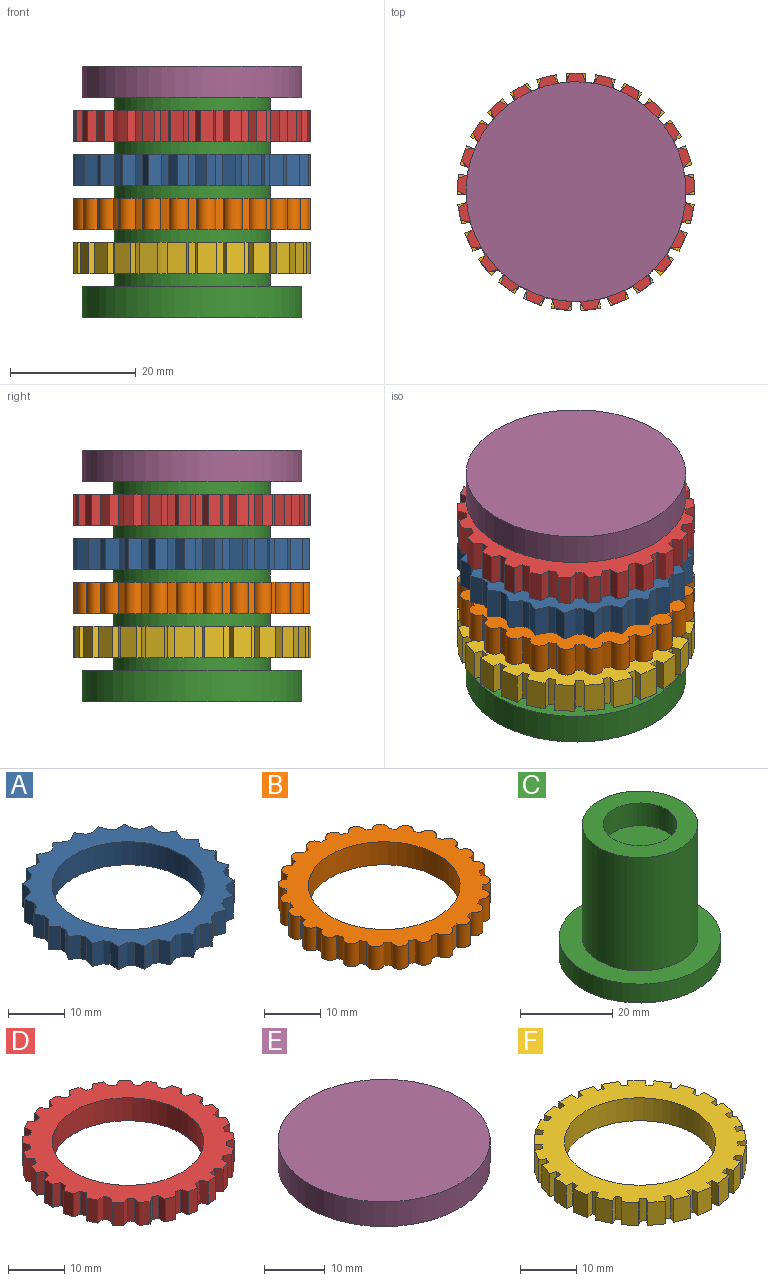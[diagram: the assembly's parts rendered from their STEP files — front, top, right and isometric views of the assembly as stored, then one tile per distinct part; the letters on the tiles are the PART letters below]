
ASSEMBLY  parts=6 mates=5
PART A: 78 faces, bbox 37.7x37.6x5 mm
  f0: plane 5x1.86mm, normal (0.5,0.87,0), area 10.8mm2, adj f1,f74,f76,f77
  f1: cylinder r=17.5mm len=5mm, axis (0,0,-1), area 6mm2, adj f0,f2,f76,f77
  f2: plane 5x2.12mm, normal (0.99,-0.17,0), area 10.8mm2, adj f1,f3,f76,f77
  f3: plane 5x2.07mm, normal (0.27,0.96,0), area 10.8mm2, adj f2,f4,f76,f77
  f4: cylinder r=17.5mm len=5mm, axis (0,0,-1), area 6mm2, adj f3,f5,f76,f77
  f5: plane 5x2.14mm, normal (1,0.08,0), area 10.8mm2, adj f4,f6,f76,f77
  f6: plane 5x2.15mm, normal (0.02,1,0), area 10.8mm2, adj f5,f7,f76,f77
  f7: cylinder r=17.5mm len=5mm, axis (0,0,-1), area 6mm2, adj f6,f8,f76,f77
  f8: plane 5x2.03mm, normal (0.94,0.33,0), area 10.8mm2, adj f7,f9,f76,f77
  f9: plane 5x2.09mm, normal (-0.23,0.97,0), area 10.8mm2, adj f8,f10,f76,f77
  f10: cylinder r=17.5mm len=5mm, axis (0,0,-1), area 6mm2, adj f9,f11,f76,f77
  f11: plane 5x1.79mm, normal (0.83,0.55,0), area 10.8mm2, adj f10,f12,f76,f77
  f12: plane 5x1.91mm, normal (-0.46,0.89,0), area 10.8mm2, adj f11,f13,f76,f77
  f13: cylinder r=17.5mm len=5mm, axis (0,0,-1), area 6mm2, adj f12,f14,f76,f77
  f14: plane 5x1.6mm, normal (0.67,0.74,0), area 10.8mm2, adj f13,f15,f76,f77
  f15: plane 5x1.6mm, normal (-0.67,0.74,0), area 10.8mm2, adj f14,f16,f76,f77
  f16: cylinder r=17.5mm len=5mm, axis (0,0,-1), area 6mm2, adj f15,f17,f76,f77
  f17: plane 5x1.91mm, normal (0.46,0.89,0), area 10.8mm2, adj f16,f18,f76,f77
  f18: plane 5x1.79mm, normal (-0.83,0.55,0), area 10.8mm2, adj f17,f19,f76,f77
  f19: cylinder r=17.5mm len=5mm, axis (0,0,-1), area 6mm2, adj f18,f20,f76,f77
  f20: plane 5x2.09mm, normal (0.23,0.97,0), area 10.8mm2, adj f19,f21,f76,f77
  f21: plane 5x2.03mm, normal (-0.94,0.33,0), area 10.8mm2, adj f20,f22,f76,f77
  f22: cylinder r=17.5mm len=5mm, axis (0,0,-1), area 6mm2, adj f21,f23,f76,f77
  f23: plane 5x2.15mm, normal (-0.02,1,0), area 10.8mm2, adj f22,f24,f76,f77
  f24: plane 5x2.14mm, normal (-1,0.08,0), area 10.8mm2, adj f23,f25,f76,f77
  f25: cylinder r=17.5mm len=5mm, axis (0,0,-1), area 6mm2, adj f24,f26,f76,f77
  f26: plane 5x2.07mm, normal (-0.27,0.96,0), area 10.8mm2, adj f25,f27,f76,f77
  f27: plane 5x2.12mm, normal (-0.99,-0.17,0), area 10.8mm2, adj f26,f28,f76,f77
  f28: cylinder r=17.5mm len=5mm, axis (0,0,-1), area 6mm2, adj f27,f29,f76,f77
  f29: plane 5x1.86mm, normal (-0.5,0.87,0), area 10.8mm2, adj f28,f30,f76,f77
  f30: plane 5x1.96mm, normal (-0.91,-0.41,0), area 10.8mm2, adj f29,f31,f76,f77
  f31: cylinder r=17.5mm len=5mm, axis (0,0,-1), area 6mm2, adj f30,f32,f76,f77
  f32: plane 5x1.54mm, normal (-0.7,0.72,0), area 10.8mm2, adj f31,f33,f76,f77
  f33: plane 5x1.68mm, normal (-0.78,-0.62,0), area 10.8mm2, adj f32,f34,f76,f77
  f34: cylinder r=17.5mm len=5mm, axis (0,0,-1), area 6mm2, adj f33,f35,f76,f77
  f35: plane 5x1.84mm, normal (-0.85,0.52,0), area 10.8mm2, adj f34,f36,f76,f77
  f36: plane 5x1.72mm, normal (-0.6,-0.8,0), area 10.8mm2, adj f35,f37,f76,f77
  f37: cylinder r=17.5mm len=5mm, axis (0,0,-1), area 6mm2, adj f36,f38,f76,f77
  f38: plane 5x2.06mm, normal (-0.96,0.29,0), area 10.8mm2, adj f37,f39,f76,f77
  f39: plane 5x1.98mm, normal (-0.39,-0.92,0), area 10.8mm2, adj f38,f40,f76,f77
  f40: cylinder r=17.5mm len=5mm, axis (0,0,-1), area 6mm2, adj f39,f41,f76,f77
  f41: plane 5x2.15mm, normal (-1,0.04,0), area 10.8mm2, adj f40,f42,f76,f77
  f42: plane 5x2.13mm, normal (-0.14,-0.99,0), area 10.8mm2, adj f41,f43,f76,f77
  f43: cylinder r=17.5mm len=5mm, axis (0,0,-1), area 6mm2, adj f42,f44,f76,f77
  f44: plane 5x2.1mm, normal (-0.98,-0.21,0), area 10.8mm2, adj f43,f45,f76,f77
  f45: plane 5x2.14mm, normal (0.11,-0.99,0), area 10.8mm2, adj f44,f46,f76,f77
  f46: cylinder r=17.5mm len=5mm, axis (0,0,-1), area 6mm2, adj f45,f47,f76,f77
  f47: plane 5x1.93mm, normal (-0.9,-0.44,0), area 10.8mm2, adj f46,f48,f76,f77
  f48: plane 5x2.02mm, normal (0.35,-0.94,0), area 10.8mm2, adj f47,f49,f76,f77
  f49: cylinder r=17.5mm len=5mm, axis (0,0,-1), area 6mm2, adj f48,f50,f76,f77
  f50: plane 5x1.63mm, normal (-0.76,-0.65,0), area 10.8mm2, adj f49,f51,f76,f77
  f51: plane 5x1.76mm, normal (0.57,-0.82,0), area 10.8mm2, adj f50,f52,f76,f77
  f52: cylinder r=17.5mm len=5mm, axis (0,0,-1), area 6mm2, adj f51,f53,f76,f77
  f53: plane 5x1.76mm, normal (-0.57,-0.82,0), area 10.8mm2, adj f52,f54,f76,f77
  f54: plane 5x1.63mm, normal (0.76,-0.65,0), area 10.8mm2, adj f53,f55,f76,f77
  f55: cylinder r=17.5mm len=5mm, axis (0,0,-1), area 6mm2, adj f54,f56,f76,f77
  f56: plane 5x2.02mm, normal (-0.35,-0.94,0), area 10.8mm2, adj f55,f57,f76,f77
  f57: plane 5x1.93mm, normal (0.9,-0.44,0), area 10.8mm2, adj f56,f58,f76,f77
  f58: cylinder r=17.5mm len=5mm, axis (0,0,-1), area 6mm2, adj f57,f59,f76,f77
  f59: plane 5x2.14mm, normal (-0.11,-0.99,0), area 10.8mm2, adj f58,f60,f76,f77
  f60: plane 5x2.1mm, normal (0.98,-0.21,0), area 10.8mm2, adj f59,f61,f76,f77
  f61: cylinder r=17.5mm len=5mm, axis (0,0,-1), area 6mm2, adj f60,f62,f76,f77
  f62: plane 5x2.13mm, normal (0.14,-0.99,0), area 10.8mm2, adj f61,f63,f76,f77
  f63: plane 5x2.15mm, normal (1,0.04,0), area 10.8mm2, adj f62,f64,f76,f77
  f64: cylinder r=17.5mm len=5mm, axis (0,0,-1), area 6mm2, adj f63,f65,f76,f77
  f65: plane 5x1.98mm, normal (0.39,-0.92,0), area 10.8mm2, adj f64,f66,f76,f77
  f66: plane 5x2.06mm, normal (0.96,0.29,0), area 10.8mm2, adj f65,f67,f76,f77
  f67: cylinder r=17.5mm len=5mm, axis (0,0,-1), area 6mm2, adj f66,f68,f76,f77
  f68: plane 5x1.72mm, normal (0.6,-0.8,0), area 10.8mm2, adj f67,f69,f76,f77
  f69: plane 5x1.84mm, normal (0.85,0.52,0), area 10.8mm2, adj f68,f70,f76,f77
  f70: cylinder r=17.5mm len=5mm, axis (0,0,-1), area 6mm2, adj f69,f71,f76,f77
  f71: plane 5x1.68mm, normal (0.78,-0.62,0), area 10.8mm2, adj f70,f72,f76,f77
  f72: plane 5x1.54mm, normal (0.7,0.72,0), area 10.8mm2, adj f71,f73,f76,f77
  f73: cylinder r=17.5mm len=5mm, axis (0,0,-1), area 6mm2, adj f72,f74,f76,f77
  f74: plane 5x1.96mm, normal (0.91,-0.41,0), area 10.8mm2, adj f0,f73,f76,f77
  f75: cylinder r=13.5mm len=27mm, axis (0,0,-1), area 424.1mm2, adj f76,f77
  f76: plane 37.66x37.59mm, normal (0,0,1), area 443.2mm2, adj f0,f1,f2,f3,f4,f5,f6,f7
  f77: plane 37.66x37.59mm, normal (0,0,-1), area 443.2mm2, adj f0,f1,f2,f3,f4,f5,f6,f7
PART B: 53 faces, bbox 37.7x37.7x5 mm
  f0: cylinder r=17.5mm len=5mm, axis (0,0,-1), area 6.9mm2, adj f1,f50,f51,f52
  f1: cylinder r=1.51mm len=5mm, axis (0,0,-1), area 23.3mm2, adj f0,f2,f51,f52
  f2: cylinder r=17.5mm len=5mm, axis (0,0,-1), area 6.9mm2, adj f1,f3,f51,f52
  f3: cylinder r=1.51mm len=5mm, axis (0,0,-1), area 23.3mm2, adj f2,f4,f51,f52
  f4: cylinder r=17.5mm len=5mm, axis (0,0,-1), area 6.9mm2, adj f3,f5,f51,f52
  f5: cylinder r=1.51mm len=5mm, axis (0,0,-1), area 23.3mm2, adj f4,f6,f51,f52
  f6: cylinder r=17.5mm len=5mm, axis (0,0,-1), area 6.9mm2, adj f5,f7,f51,f52
  f7: cylinder r=1.51mm len=5mm, axis (0,0,-1), area 23.3mm2, adj f6,f8,f51,f52
  f8: cylinder r=17.5mm len=5mm, axis (0,0,-1), area 6.9mm2, adj f7,f9,f51,f52
  f9: cylinder r=1.51mm len=5mm, axis (0,0,-1), area 23.3mm2, adj f8,f10,f51,f52
  f10: cylinder r=17.5mm len=5mm, axis (0,0,-1), area 6.9mm2, adj f9,f11,f51,f52
  f11: cylinder r=1.51mm len=5mm, axis (0,0,-1), area 23.3mm2, adj f10,f12,f51,f52
  f12: cylinder r=17.5mm len=5mm, axis (0,0,-1), area 6.9mm2, adj f11,f13,f51,f52
  f13: cylinder r=1.51mm len=5mm, axis (0,0,-1), area 23.3mm2, adj f12,f14,f51,f52
  f14: cylinder r=17.5mm len=5mm, axis (0,0,-1), area 6.9mm2, adj f13,f15,f51,f52
  f15: cylinder r=1.51mm len=5mm, axis (0,0,-1), area 23.3mm2, adj f14,f16,f51,f52
  f16: cylinder r=17.5mm len=5mm, axis (0,0,-1), area 6.9mm2, adj f15,f17,f51,f52
  f17: cylinder r=1.51mm len=5mm, axis (0,0,-1), area 23.3mm2, adj f16,f18,f51,f52
  f18: cylinder r=17.5mm len=5mm, axis (0,0,-1), area 6.9mm2, adj f17,f19,f51,f52
  f19: cylinder r=1.51mm len=5mm, axis (0,0,-1), area 23.3mm2, adj f18,f20,f51,f52
  f20: cylinder r=17.5mm len=5mm, axis (0,0,-1), area 6.9mm2, adj f19,f21,f51,f52
  f21: cylinder r=1.51mm len=5mm, axis (0,0,-1), area 23.3mm2, adj f20,f22,f51,f52
  f22: cylinder r=17.5mm len=5mm, axis (0,0,-1), area 6.9mm2, adj f21,f23,f51,f52
  f23: cylinder r=1.51mm len=5mm, axis (0,0,-1), area 23.3mm2, adj f22,f24,f51,f52
  f24: cylinder r=17.5mm len=5mm, axis (0,0,-1), area 6.9mm2, adj f23,f25,f51,f52
  f25: cylinder r=1.51mm len=5mm, axis (0,0,-1), area 23.3mm2, adj f24,f26,f51,f52
  f26: cylinder r=17.5mm len=5mm, axis (0,0,-1), area 6.9mm2, adj f25,f27,f51,f52
  f27: cylinder r=1.51mm len=5mm, axis (0,0,-1), area 23.3mm2, adj f26,f28,f51,f52
  f28: cylinder r=17.5mm len=5mm, axis (0,0,-1), area 6.9mm2, adj f27,f29,f51,f52
  f29: cylinder r=1.51mm len=5mm, axis (0,0,-1), area 23.3mm2, adj f28,f30,f51,f52
  f30: cylinder r=17.5mm len=5mm, axis (0,0,-1), area 6.9mm2, adj f29,f31,f51,f52
  f31: cylinder r=1.51mm len=5mm, axis (0,0,-1), area 23.3mm2, adj f30,f32,f51,f52
  f32: cylinder r=17.5mm len=5mm, axis (0,0,-1), area 6.9mm2, adj f31,f33,f51,f52
  f33: cylinder r=1.51mm len=5mm, axis (0,0,-1), area 23.3mm2, adj f32,f34,f51,f52
  f34: cylinder r=17.5mm len=5mm, axis (0,0,-1), area 6.9mm2, adj f33,f35,f51,f52
  f35: cylinder r=1.51mm len=5mm, axis (0,0,-1), area 23.3mm2, adj f34,f36,f51,f52
  f36: cylinder r=17.5mm len=5mm, axis (0,0,-1), area 6.9mm2, adj f35,f37,f51,f52
  f37: cylinder r=1.51mm len=5mm, axis (0,0,-1), area 23.3mm2, adj f36,f38,f51,f52
  f38: cylinder r=17.5mm len=5mm, axis (0,0,-1), area 6.9mm2, adj f37,f39,f51,f52
  f39: cylinder r=1.51mm len=5mm, axis (0,0,-1), area 23.3mm2, adj f38,f40,f51,f52
  f40: cylinder r=17.5mm len=5mm, axis (0,0,-1), area 6.9mm2, adj f39,f41,f51,f52
  f41: cylinder r=1.51mm len=5mm, axis (0,0,-1), area 23.3mm2, adj f40,f42,f51,f52
  f42: cylinder r=17.5mm len=5mm, axis (0,0,-1), area 6.9mm2, adj f41,f43,f51,f52
  f43: cylinder r=1.51mm len=5mm, axis (0,0,-1), area 23.3mm2, adj f42,f44,f51,f52
  f44: cylinder r=17.5mm len=5mm, axis (0,0,-1), area 6.9mm2, adj f43,f45,f51,f52
  f45: cylinder r=1.51mm len=5mm, axis (0,0,-1), area 23.3mm2, adj f44,f46,f51,f52
  f46: cylinder r=17.5mm len=5mm, axis (0,0,-1), area 6.9mm2, adj f45,f47,f51,f52
  f47: cylinder r=1.51mm len=5mm, axis (0,0,-1), area 23.3mm2, adj f46,f48,f51,f52
  f48: cylinder r=17.5mm len=5mm, axis (0,0,-1), area 6.9mm2, adj f47,f50,f51,f52
  f49: cylinder r=13.5mm len=27mm, axis (0,0,-1), area 424.1mm2, adj f51,f52
  f50: cylinder r=1.51mm len=5mm, axis (0,0,-1), area 23.3mm2, adj f0,f48,f51,f52
  f51: plane 37.74x37.68mm, normal (0,0,1), area 472.5mm2, adj f0,f1,f2,f3,f4,f5,f6,f7
  f52: plane 37.74x37.68mm, normal (0,0,-1), area 472.5mm2, adj f0,f1,f2,f3,f4,f5,f6,f7
PART C: 7 faces, bbox 35x35x35 mm
  f0: cylinder r=17.5mm len=35mm, axis (0,0,-1), area 549.8mm2, adj f1,f2
  f1: plane 35x35mm, normal (0,0,1), area 471.2mm2, adj f0,f3
  f2: plane 35x35mm, normal (0,0,-1), area 962.1mm2, adj f0
  f3: cylinder r=12.5mm len=30mm, axis (0,0,-1), area 2356.2mm2, adj f1,f4
  f4: plane 25x25mm, normal (0,0,1), area 289.8mm2, adj f3,f5
  f5: cylinder r=8mm len=16mm, axis (0,0,1), area 301.6mm2, adj f4,f6
  f6: plane 16x16mm, normal (0,0,1), area 201.1mm2, adj f5
PART D: 103 faces, bbox 37.8x37.7x5 mm
  f0: plane 5x1.55mm, normal (0.08,1,0), area 7.8mm2, adj f1,f99,f101,f102
  f1: cylinder r=17.5mm len=5mm, axis (0,0,-1), area 6.1mm2, adj f0,f2,f101,f102
  f2: plane 5x1.27mm, normal (0.82,-0.58,0), area 7.8mm2, adj f1,f3,f101,f102
  f3: plane 5x1.67mm, normal (0.84,0.54,0), area 9.9mm2, adj f2,f4,f101,f102
  f4: plane 5x1.53mm, normal (-0.17,0.99,0), area 7.8mm2, adj f3,f5,f101,f102
  f5: cylinder r=17.5mm len=5mm, axis (0,0,-1), area 6.1mm2, adj f4,f6,f101,f102
  f6: plane 5x1.46mm, normal (0.94,-0.35,0), area 7.8mm2, adj f5,f7,f101,f102
  f7: plane 5x1.44mm, normal (0.68,0.73,0), area 9.9mm2, adj f6,f8,f101,f102
  f8: plane 5x1.42mm, normal (-0.41,0.91,0), area 7.8mm2, adj f7,f9,f101,f102
  f9: cylinder r=17.5mm len=5mm, axis (0,0,-1), area 6.1mm2, adj f8,f10,f101,f102
  f10: plane 5x1.55mm, normal (0.99,-0.11,0), area 7.8mm2, adj f9,f11,f101,f102
  f11: plane 5x1.73mm, normal (0.48,0.88,0), area 9.9mm2, adj f10,f12,f101,f102
  f12: plane 5x1.21mm, normal (-0.63,0.78,0), area 7.8mm2, adj f11,f13,f101,f102
  f13: cylinder r=17.5mm len=5mm, axis (0,0,-1), area 6.1mm2, adj f12,f14,f101,f102
  f14: plane 5x1.54mm, normal (0.99,0.14,0), area 7.8mm2, adj f13,f15,f101,f102
  f15: plane 5x1.91mm, normal (0.25,0.97,0), area 9.9mm2, adj f14,f16,f101,f102
  f16: plane 5x1.24mm, normal (-0.8,0.6,0), area 7.8mm2, adj f15,f17,f101,f102
  f17: cylinder r=17.5mm len=5mm, axis (0,0,-1), area 6.1mm2, adj f16,f18,f101,f102
  f18: plane 5x1.44mm, normal (0.92,0.38,0), area 7.8mm2, adj f17,f19,f101,f102
  f19: plane 5x1.98mm, normal (0,1,0), area 9.9mm2, adj f18,f20,f101,f102
  f20: plane 5x1.44mm, normal (-0.92,0.38,0), area 7.8mm2, adj f19,f21,f101,f102
  f21: cylinder r=17.5mm len=5mm, axis (0,0,-1), area 6.1mm2, adj f20,f22,f101,f102
  f22: plane 5x1.24mm, normal (0.8,0.6,0), area 7.8mm2, adj f21,f23,f101,f102
  f23: plane 5x1.91mm, normal (-0.25,0.97,0), area 9.9mm2, adj f22,f24,f101,f102
  f24: plane 5x1.54mm, normal (-0.99,0.14,0), area 7.8mm2, adj f23,f25,f101,f102
  f25: cylinder r=17.5mm len=5mm, axis (0,0,-1), area 6.1mm2, adj f24,f26,f101,f102
  f26: plane 5x1.21mm, normal (0.63,0.78,0), area 7.8mm2, adj f25,f27,f101,f102
  f27: plane 5x1.73mm, normal (-0.48,0.88,0), area 9.9mm2, adj f26,f28,f101,f102
  f28: plane 5x1.55mm, normal (-0.99,-0.11,0), area 7.8mm2, adj f27,f29,f101,f102
  f29: cylinder r=17.5mm len=5mm, axis (0,0,-1), area 6.1mm2, adj f28,f30,f101,f102
  f30: plane 5x1.42mm, normal (0.41,0.91,0), area 7.8mm2, adj f29,f31,f101,f102
  f31: plane 5x1.44mm, normal (-0.68,0.73,0), area 9.9mm2, adj f30,f32,f101,f102
  f32: plane 5x1.46mm, normal (-0.94,-0.35,0), area 7.8mm2, adj f31,f33,f101,f102
  f33: cylinder r=17.5mm len=5mm, axis (0,0,-1), area 6.1mm2, adj f32,f34,f101,f102
  f34: plane 5x1.53mm, normal (0.17,0.99,0), area 7.8mm2, adj f33,f35,f101,f102
  f35: plane 5x1.67mm, normal (-0.84,0.54,0), area 9.9mm2, adj f34,f36,f101,f102
  f36: plane 5x1.27mm, normal (-0.82,-0.58,0), area 7.8mm2, adj f35,f37,f101,f102
  f37: cylinder r=17.5mm len=5mm, axis (0,0,-1), area 6.1mm2, adj f36,f38,f101,f102
  f38: plane 5x1.55mm, normal (-0.08,1,0), area 7.8mm2, adj f37,f39,f101,f102
  f39: plane 5x1.88mm, normal (-0.95,0.31,0), area 9.9mm2, adj f38,f40,f101,f102
  f40: plane 5x1.18mm, normal (-0.65,-0.76,0), area 7.8mm2, adj f39,f41,f101,f102
  f41: cylinder r=17.5mm len=5mm, axis (0,0,-1), area 6.1mm2, adj f40,f42,f101,f102
  f42: plane 5x1.47mm, normal (-0.32,0.95,0), area 7.8mm2, adj f41,f43,f101,f102
  f43: plane 5x1.97mm, normal (-1,0.06,0), area 9.9mm2, adj f42,f44,f101,f102
  f44: plane 5x1.4mm, normal (-0.44,-0.9,0), area 7.8mm2, adj f43,f45,f101,f102
  f45: cylinder r=17.5mm len=5mm, axis (0,0,-1), area 6.1mm2, adj f44,f46,f101,f102
  f46: plane 5x1.3mm, normal (-0.55,0.84,0), area 7.8mm2, adj f45,f47,f101,f102
  f47: plane 5x1.94mm, normal (-0.98,-0.19,0), area 9.9mm2, adj f46,f48,f101,f102
  f48: plane 5x1.52mm, normal (-0.2,-0.98,0), area 7.8mm2, adj f47,f49,f101,f102
  f49: cylinder r=17.5mm len=5mm, axis (0,0,-1), area 6.1mm2, adj f48,f50,f101,f102
  f50: plane 5x1.15mm, normal (-0.74,0.67,0), area 7.8mm2, adj f49,f51,f101,f102
  f51: plane 5x1.79mm, normal (-0.9,-0.43,0), area 9.9mm2, adj f50,f52,f101,f102
  f52: plane 5x1.55mm, normal (0.05,-1,0), area 7.8mm2, adj f51,f53,f101,f102
  f53: cylinder r=17.5mm len=5mm, axis (0,0,-1), area 6.1mm2, adj f52,f54,f101,f102
  f54: plane 5x1.37mm, normal (-0.88,0.47,0), area 7.8mm2, adj f53,f55,f101,f102
  f55: plane 5x1.52mm, normal (-0.77,-0.64,0), area 9.9mm2, adj f54,f56,f101,f102
  f56: plane 5x1.49mm, normal (0.29,-0.96,0), area 7.8mm2, adj f55,f57,f101,f102
  f57: cylinder r=17.5mm len=5mm, axis (0,0,-1), area 6.1mm2, adj f56,f58,f101,f102
  f58: plane 5x1.51mm, normal (-0.97,0.23,0), area 7.8mm2, adj f57,f59,f101,f102
  f59: plane 5x1.6mm, normal (-0.59,-0.81,0), area 9.9mm2, adj f58,f60,f101,f102
  f60: plane 5x1.33mm, normal (0.52,-0.85,0), area 7.8mm2, adj f59,f61,f101,f102
  f61: cylinder r=17.5mm len=5mm, axis (0,0,-1), area 6.1mm2, adj f60,f62,f101,f102
  f62: plane 5x1.56mm, normal (-1,-0.02,0), area 7.8mm2, adj f61,f63,f101,f102
  f63: plane 5x1.84mm, normal (-0.37,-0.93,0), area 9.9mm2, adj f62,f64,f101,f102
  f64: plane 5x1.12mm, normal (0.72,-0.7,0), area 7.8mm2, adj f63,f65,f101,f102
  f65: cylinder r=17.5mm len=5mm, axis (0,0,-1), area 6.1mm2, adj f64,f66,f101,f102
  f66: plane 5x1.5mm, normal (-0.96,-0.26,0), area 7.8mm2, adj f65,f67,f101,f102
  f67: plane 5x1.96mm, normal (-0.13,-0.99,0), area 9.9mm2, adj f66,f68,f101,f102
  f68: plane 5x1.35mm, normal (0.87,-0.5,0), area 7.8mm2, adj f67,f69,f101,f102
  f69: cylinder r=17.5mm len=5mm, axis (0,0,-1), area 6.1mm2, adj f68,f70,f101,f102
  f70: plane 5x1.35mm, normal (-0.87,-0.5,0), area 7.8mm2, adj f69,f71,f101,f102
  f71: plane 5x1.96mm, normal (0.13,-0.99,0), area 9.9mm2, adj f70,f72,f101,f102
  f72: plane 5x1.5mm, normal (0.96,-0.26,0), area 7.8mm2, adj f71,f73,f101,f102
  f73: cylinder r=17.5mm len=5mm, axis (0,0,-1), area 6.1mm2, adj f72,f74,f101,f102
  f74: plane 5x1.12mm, normal (-0.72,-0.7,0), area 7.8mm2, adj f73,f75,f101,f102
  f75: plane 5x1.84mm, normal (0.37,-0.93,0), area 9.9mm2, adj f74,f76,f101,f102
  f76: plane 5x1.56mm, normal (1,-0.02,0), area 7.8mm2, adj f75,f77,f101,f102
  f77: cylinder r=17.5mm len=5mm, axis (0,0,-1), area 6.1mm2, adj f76,f78,f101,f102
  f78: plane 5x1.33mm, normal (-0.52,-0.85,0), area 7.8mm2, adj f77,f79,f101,f102
  f79: plane 5x1.6mm, normal (0.59,-0.81,0), area 9.9mm2, adj f78,f80,f101,f102
  f80: plane 5x1.51mm, normal (0.97,0.23,0), area 7.8mm2, adj f79,f81,f101,f102
  f81: cylinder r=17.5mm len=5mm, axis (0,0,-1), area 6.1mm2, adj f80,f82,f101,f102
  f82: plane 5x1.49mm, normal (-0.29,-0.96,0), area 7.8mm2, adj f81,f83,f101,f102
  f83: plane 5x1.52mm, normal (0.77,-0.64,0), area 9.9mm2, adj f82,f84,f101,f102
  f84: plane 5x1.37mm, normal (0.88,0.47,0), area 7.8mm2, adj f83,f85,f101,f102
  f85: cylinder r=17.5mm len=5mm, axis (0,0,-1), area 6.1mm2, adj f84,f86,f101,f102
  f86: plane 5x1.55mm, normal (-0.05,-1,0), area 7.8mm2, adj f85,f87,f101,f102
  f87: plane 5x1.79mm, normal (0.9,-0.43,0), area 9.9mm2, adj f86,f88,f101,f102
  f88: plane 5x1.15mm, normal (0.74,0.67,0), area 7.8mm2, adj f87,f89,f101,f102
  f89: cylinder r=17.5mm len=5mm, axis (0,0,-1), area 6.1mm2, adj f88,f90,f101,f102
  f90: plane 5x1.52mm, normal (0.2,-0.98,0), area 7.8mm2, adj f89,f91,f101,f102
  f91: plane 5x1.94mm, normal (0.98,-0.19,0), area 9.9mm2, adj f90,f92,f101,f102
  f92: plane 5x1.3mm, normal (0.55,0.84,0), area 7.8mm2, adj f91,f93,f101,f102
  f93: cylinder r=17.5mm len=5mm, axis (0,0,-1), area 6.1mm2, adj f92,f94,f101,f102
  f94: plane 5x1.4mm, normal (0.44,-0.9,0), area 7.8mm2, adj f93,f95,f101,f102
  f95: plane 5x1.97mm, normal (1,0.06,0), area 9.9mm2, adj f94,f96,f101,f102
  f96: plane 5x1.47mm, normal (0.32,0.95,0), area 7.8mm2, adj f95,f97,f101,f102
  f97: cylinder r=17.5mm len=5mm, axis (0,0,-1), area 6.1mm2, adj f96,f98,f101,f102
  f98: plane 5x1.18mm, normal (0.65,-0.76,0), area 7.8mm2, adj f97,f99,f101,f102
  f99: plane 5x1.88mm, normal (0.95,0.31,0), area 9.9mm2, adj f0,f98,f101,f102
  f100: cylinder r=13.5mm len=27mm, axis (0,0,-1), area 424.1mm2, adj f101,f102
  f101: plane 37.78x37.71mm, normal (0,0,1), area 478.2mm2, adj f0,f1,f2,f3,f4,f5,f6,f7
  f102: plane 37.78x37.71mm, normal (0,0,-1), area 478.2mm2, adj f0,f1,f2,f3,f4,f5,f6,f7
PART E: 5 faces, bbox 35x35x10 mm
  f0: cylinder r=7.85mm len=15.7mm, axis (0,0,1), area 246.6mm2, adj f1,f4
  f1: plane 15.7x15.7mm, normal (0,0,-1), area 193.6mm2, adj f0
  f2: cylinder r=17.5mm len=35mm, axis (0,0,-1), area 549.8mm2, adj f3,f4
  f3: plane 35x35mm, normal (0,0,1), area 962.1mm2, adj f2
  f4: plane 35x35mm, normal (0,0,-1), area 768.5mm2, adj f0,f2
PART F: 103 faces, bbox 37.9x37.8x5 mm
  f0: plane 5x1.37mm, normal (-0.31,0.95,0), area 7.2mm2, adj f1,f99,f101,f102
  f1: cylinder r=17.5mm len=5mm, axis (0,0,-1), area 6.2mm2, adj f0,f2,f101,f102
  f2: plane 5x1.21mm, normal (0.54,-0.84,0), area 7.2mm2, adj f1,f3,f101,f102
  f3: plane 5x2.66mm, normal (0.84,0.54,0), area 15.7mm2, adj f2,f4,f101,f102
  f4: plane 5x1.21mm, normal (-0.54,0.84,0), area 7.2mm2, adj f3,f5,f101,f102
  f5: cylinder r=17.5mm len=5mm, axis (0,0,-1), area 6.2mm2, adj f4,f6,f101,f102
  f6: plane 5x1.05mm, normal (0.73,-0.68,0), area 7.2mm2, adj f5,f7,f101,f102
  f7: plane 5x2.3mm, normal (0.68,0.73,0), area 15.7mm2, adj f6,f8,f101,f102
  f8: plane 5x1.05mm, normal (-0.73,0.68,0), area 7.2mm2, adj f7,f9,f101,f102
  f9: cylinder r=17.5mm len=5mm, axis (0,0,-1), area 6.2mm2, adj f8,f10,f101,f102
  f10: plane 5x1.26mm, normal (0.88,-0.48,0), area 7.2mm2, adj f9,f11,f101,f102
  f11: plane 5x2.76mm, normal (0.48,0.88,0), area 15.7mm2, adj f10,f12,f101,f102
  f12: plane 5x1.26mm, normal (-0.88,0.48,0), area 7.2mm2, adj f11,f13,f101,f102
  f13: cylinder r=17.5mm len=5mm, axis (0,0,-1), area 6.2mm2, adj f12,f14,f101,f102
  f14: plane 5x1.39mm, normal (0.97,-0.25,0), area 7.2mm2, adj f13,f15,f101,f102
  f15: plane 5x3.05mm, normal (0.25,0.97,0), area 15.7mm2, adj f14,f16,f101,f102
  f16: plane 5x1.39mm, normal (-0.97,0.25,0), area 7.2mm2, adj f15,f17,f101,f102
  f17: cylinder r=17.5mm len=5mm, axis (0,0,-1), area 6.2mm2, adj f16,f18,f101,f102
  f18: plane 5x1.44mm, normal (1,0,0), area 7.2mm2, adj f17,f19,f101,f102
  f19: plane 5x3.15mm, normal (0,1,0), area 15.7mm2, adj f18,f20,f101,f102
  f20: plane 5x1.44mm, normal (-1,0,0), area 7.2mm2, adj f19,f21,f101,f102
  f21: cylinder r=17.5mm len=5mm, axis (0,0,-1), area 6.2mm2, adj f20,f22,f101,f102
  f22: plane 5x1.39mm, normal (0.97,0.25,0), area 7.2mm2, adj f21,f23,f101,f102
  f23: plane 5x3.05mm, normal (-0.25,0.97,0), area 15.7mm2, adj f22,f24,f101,f102
  f24: plane 5x1.39mm, normal (-0.97,-0.25,0), area 7.2mm2, adj f23,f25,f101,f102
  f25: cylinder r=17.5mm len=5mm, axis (0,0,-1), area 6.2mm2, adj f24,f26,f101,f102
  f26: plane 5x1.26mm, normal (0.88,0.48,0), area 7.2mm2, adj f25,f27,f101,f102
  f27: plane 5x2.76mm, normal (-0.48,0.88,0), area 15.7mm2, adj f26,f28,f101,f102
  f28: plane 5x1.26mm, normal (-0.88,-0.48,0), area 7.2mm2, adj f27,f29,f101,f102
  f29: cylinder r=17.5mm len=5mm, axis (0,0,-1), area 6.2mm2, adj f28,f30,f101,f102
  f30: plane 5x1.05mm, normal (0.73,0.68,0), area 7.2mm2, adj f29,f31,f101,f102
  f31: plane 5x2.3mm, normal (-0.68,0.73,0), area 15.7mm2, adj f30,f32,f101,f102
  f32: plane 5x1.05mm, normal (-0.73,-0.68,0), area 7.2mm2, adj f31,f33,f101,f102
  f33: cylinder r=17.5mm len=5mm, axis (0,0,-1), area 6.2mm2, adj f32,f34,f101,f102
  f34: plane 5x1.21mm, normal (0.54,0.84,0), area 7.2mm2, adj f33,f35,f101,f102
  f35: plane 5x2.66mm, normal (-0.84,0.54,0), area 15.7mm2, adj f34,f36,f101,f102
  f36: plane 5x1.21mm, normal (-0.54,-0.84,0), area 7.2mm2, adj f35,f37,f101,f102
  f37: cylinder r=17.5mm len=5mm, axis (0,0,-1), area 6.2mm2, adj f36,f38,f101,f102
  f38: plane 5x1.37mm, normal (0.31,0.95,0), area 7.2mm2, adj f37,f39,f101,f102
  f39: plane 5x2.99mm, normal (-0.95,0.31,0), area 15.7mm2, adj f38,f40,f101,f102
  f40: plane 5x1.37mm, normal (-0.31,-0.95,0), area 7.2mm2, adj f39,f41,f101,f102
  f41: cylinder r=17.5mm len=5mm, axis (0,0,-1), area 6.2mm2, adj f40,f42,f101,f102
  f42: plane 5x1.43mm, normal (0.06,1,0), area 7.2mm2, adj f41,f43,f101,f102
  f43: plane 5x3.14mm, normal (-1,0.06,0), area 15.7mm2, adj f42,f44,f101,f102
  f44: plane 5x1.43mm, normal (-0.06,-1,0), area 7.2mm2, adj f43,f45,f101,f102
  f45: cylinder r=17.5mm len=5mm, axis (0,0,-1), area 6.2mm2, adj f44,f46,f101,f102
  f46: plane 5x1.41mm, normal (-0.19,0.98,0), area 7.2mm2, adj f45,f47,f101,f102
  f47: plane 5x3.09mm, normal (-0.98,-0.19,0), area 15.7mm2, adj f46,f48,f101,f102
  f48: plane 5x1.41mm, normal (0.19,-0.98,0), area 7.2mm2, adj f47,f49,f101,f102
  f49: cylinder r=17.5mm len=5mm, axis (0,0,-1), area 6.2mm2, adj f48,f50,f101,f102
  f50: plane 5x1.3mm, normal (-0.43,0.9,0), area 7.2mm2, adj f49,f51,f101,f102
  f51: plane 5x2.85mm, normal (-0.9,-0.43,0), area 15.7mm2, adj f50,f52,f101,f102
  f52: plane 5x1.3mm, normal (0.43,-0.9,0), area 7.2mm2, adj f51,f53,f101,f102
  f53: cylinder r=17.5mm len=5mm, axis (0,0,-1), area 6.2mm2, adj f52,f54,f101,f102
  f54: plane 5x1.11mm, normal (-0.64,0.77,0), area 7.2mm2, adj f53,f55,f101,f102
  f55: plane 5x2.43mm, normal (-0.77,-0.64,0), area 15.7mm2, adj f54,f56,f101,f102
  f56: plane 5x1.11mm, normal (0.64,-0.77,0), area 7.2mm2, adj f55,f57,f101,f102
  f57: cylinder r=17.5mm len=5mm, axis (0,0,-1), area 6.2mm2, adj f56,f58,f101,f102
  f58: plane 5x1.16mm, normal (-0.81,0.59,0), area 7.2mm2, adj f57,f59,f101,f102
  f59: plane 5x2.55mm, normal (-0.59,-0.81,0), area 15.7mm2, adj f58,f60,f101,f102
  f60: plane 5x1.16mm, normal (0.81,-0.59,0), area 7.2mm2, adj f59,f61,f101,f102
  f61: cylinder r=17.5mm len=5mm, axis (0,0,-1), area 6.2mm2, adj f60,f62,f101,f102
  f62: plane 5x1.34mm, normal (-0.93,0.37,0), area 7.2mm2, adj f61,f63,f101,f102
  f63: plane 5x2.93mm, normal (-0.37,-0.93,0), area 15.7mm2, adj f62,f64,f101,f102
  f64: plane 5x1.34mm, normal (0.93,-0.37,0), area 7.2mm2, adj f63,f65,f101,f102
  f65: cylinder r=17.5mm len=5mm, axis (0,0,-1), area 6.2mm2, adj f64,f66,f101,f102
  f66: plane 5x1.42mm, normal (-0.99,0.13,0), area 7.2mm2, adj f65,f67,f101,f102
  f67: plane 5x3.12mm, normal (-0.13,-0.99,0), area 15.7mm2, adj f66,f68,f101,f102
  f68: plane 5x1.42mm, normal (0.99,-0.13,0), area 7.2mm2, adj f67,f69,f101,f102
  f69: cylinder r=17.5mm len=5mm, axis (0,0,-1), area 6.2mm2, adj f68,f70,f101,f102
  f70: plane 5x1.42mm, normal (-0.99,-0.13,0), area 7.2mm2, adj f69,f71,f101,f102
  f71: plane 5x3.12mm, normal (0.13,-0.99,0), area 15.7mm2, adj f70,f72,f101,f102
  f72: plane 5x1.42mm, normal (0.99,0.13,0), area 7.2mm2, adj f71,f73,f101,f102
  f73: cylinder r=17.5mm len=5mm, axis (0,0,-1), area 6.2mm2, adj f72,f74,f101,f102
  f74: plane 5x1.34mm, normal (-0.93,-0.37,0), area 7.2mm2, adj f73,f75,f101,f102
  f75: plane 5x2.93mm, normal (0.37,-0.93,0), area 15.7mm2, adj f74,f76,f101,f102
  f76: plane 5x1.34mm, normal (0.93,0.37,0), area 7.2mm2, adj f75,f77,f101,f102
  f77: cylinder r=17.5mm len=5mm, axis (0,0,-1), area 6.2mm2, adj f76,f78,f101,f102
  f78: plane 5x1.16mm, normal (-0.81,-0.59,0), area 7.2mm2, adj f77,f79,f101,f102
  f79: plane 5x2.55mm, normal (0.59,-0.81,0), area 15.7mm2, adj f78,f80,f101,f102
  f80: plane 5x1.16mm, normal (0.81,0.59,0), area 7.2mm2, adj f79,f81,f101,f102
  f81: cylinder r=17.5mm len=5mm, axis (0,0,-1), area 6.2mm2, adj f80,f82,f101,f102
  f82: plane 5x1.11mm, normal (-0.64,-0.77,0), area 7.2mm2, adj f81,f83,f101,f102
  f83: plane 5x2.43mm, normal (0.77,-0.64,0), area 15.7mm2, adj f82,f84,f101,f102
  f84: plane 5x1.11mm, normal (0.64,0.77,0), area 7.2mm2, adj f83,f85,f101,f102
  f85: cylinder r=17.5mm len=5mm, axis (0,0,-1), area 6.2mm2, adj f84,f86,f101,f102
  f86: plane 5x1.3mm, normal (-0.43,-0.9,0), area 7.2mm2, adj f85,f87,f101,f102
  f87: plane 5x2.85mm, normal (0.9,-0.43,0), area 15.7mm2, adj f86,f88,f101,f102
  f88: plane 5x1.3mm, normal (0.43,0.9,0), area 7.2mm2, adj f87,f89,f101,f102
  f89: cylinder r=17.5mm len=5mm, axis (0,0,-1), area 6.2mm2, adj f88,f90,f101,f102
  f90: plane 5x1.41mm, normal (-0.19,-0.98,0), area 7.2mm2, adj f89,f91,f101,f102
  f91: plane 5x3.09mm, normal (0.98,-0.19,0), area 15.7mm2, adj f90,f92,f101,f102
  f92: plane 5x1.41mm, normal (0.19,0.98,0), area 7.2mm2, adj f91,f93,f101,f102
  f93: cylinder r=17.5mm len=5mm, axis (0,0,-1), area 6.2mm2, adj f92,f94,f101,f102
  f94: plane 5x1.43mm, normal (0.06,-1,0), area 7.2mm2, adj f93,f95,f101,f102
  f95: plane 5x3.14mm, normal (1,0.06,0), area 15.7mm2, adj f94,f96,f101,f102
  f96: plane 5x1.43mm, normal (-0.06,1,0), area 7.2mm2, adj f95,f97,f101,f102
  f97: cylinder r=17.5mm len=5mm, axis (0,0,-1), area 6.2mm2, adj f96,f98,f101,f102
  f98: plane 5x1.37mm, normal (0.31,-0.95,0), area 7.2mm2, adj f97,f99,f101,f102
  f99: plane 5x2.99mm, normal (0.95,0.31,0), area 15.7mm2, adj f0,f98,f101,f102
  f100: cylinder r=13.5mm len=27mm, axis (0,0,-1), area 424.1mm2, adj f101,f102
  f101: plane 37.85x37.78mm, normal (0,0,1), area 498.9mm2, adj f0,f1,f2,f3,f4,f5,f6,f7
  f102: plane 37.85x37.78mm, normal (0,0,-1), area 498.9mm2, adj f0,f1,f2,f3,f4,f5,f6,f7
PLACE A t=(-13.22,-3.65,-8.52)mm
PLACE B t=(-13.22,-3.65,-3.52)mm
PLACE C t=(-13.22,-3.65,-11.52)mm
PLACE D t=(-13.22,-3.65,-7.52)mm
PLACE E t=(-13.22,-3.65,-11.52)mm
PLACE F t=(-13.22,-3.65,-16.52)mm
MATE revolute B.f49 <-> C.f0  axis (0,0,1) through (-13.22,-3.65,7.48)mm
MATE revolute D.f93 <-> C.f0  axis (0,0,1) through (-13.22,-3.65,21.48)mm
MATE revolute A.f40 <-> C.f0  axis (0,0,1) through (-13.22,-3.65,14.48)mm
MATE revolute F.f9 <-> C.f0  axis (0,0,1) through (-13.22,-3.65,0.48)mm
MATE fastened E.f2 <-> C.f3  axis (0,0,-1) through (-13.22,-3.65,23.48)mm
